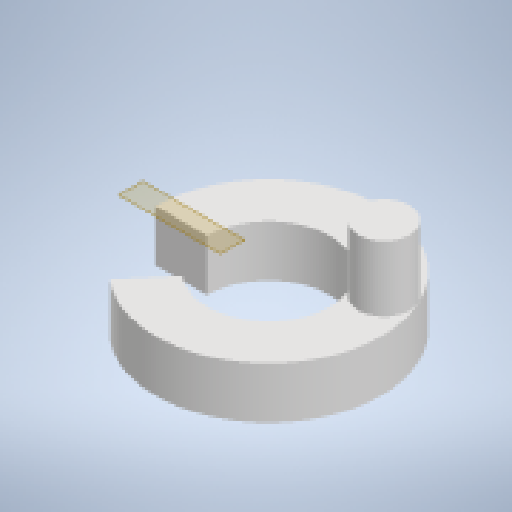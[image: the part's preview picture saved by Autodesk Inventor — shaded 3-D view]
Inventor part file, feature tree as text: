
AUTODESK INVENTOR PART (.ipt)
format: ipt  version: 2023.3 (Build 273359000, 359)  size: 159,744 bytes
history: native  units: mm
features: reference x4, other x3, sketch x2, revolve x1, plane x1, extrude x1
ambient origin geometry x8: Origin, YZ Plane, XZ Plane, XY Plane, X Axis, Y Axis, Z Axis, Center Point
bodies: Solid1 (feature_tree)
feature tree (12):
  revolve  "Revolution1"  [1 undecoded]
  plane  "Work Plane1"
  extrude  "Extrusion3"  Depth=15.0mm
  sketch  "Sketch1"  dims[d2=20.0mm d3=54.105207mm]
  reference  "Reference2"
  reference  "Reference3"
  reference  "Reference4"
  reference  "Reference5"
  sketch  "Sketch4"  dims[d8=0.7mm d9=0.7mm d10=0.7mm d11=0.7mm d15=11.808mm d16=8.435153mm d17=15.0mm d18=0.0mm]
  parser-record x1  (decoder bookkeeping rows leaked as tree rows — omitted from the tree; the rows remain in map.json)
  other  "washing_assembly.iam"
  other  "np2_washing_arm:1"
note: 1 file-system path scrubbed to <path> (originals preserved in map.json)
note: 1 required parameter value undecoded (feature->parameter linkage not recoverable at this tier; creation-order binding heuristic only, values carry confidence <= 0.55)
